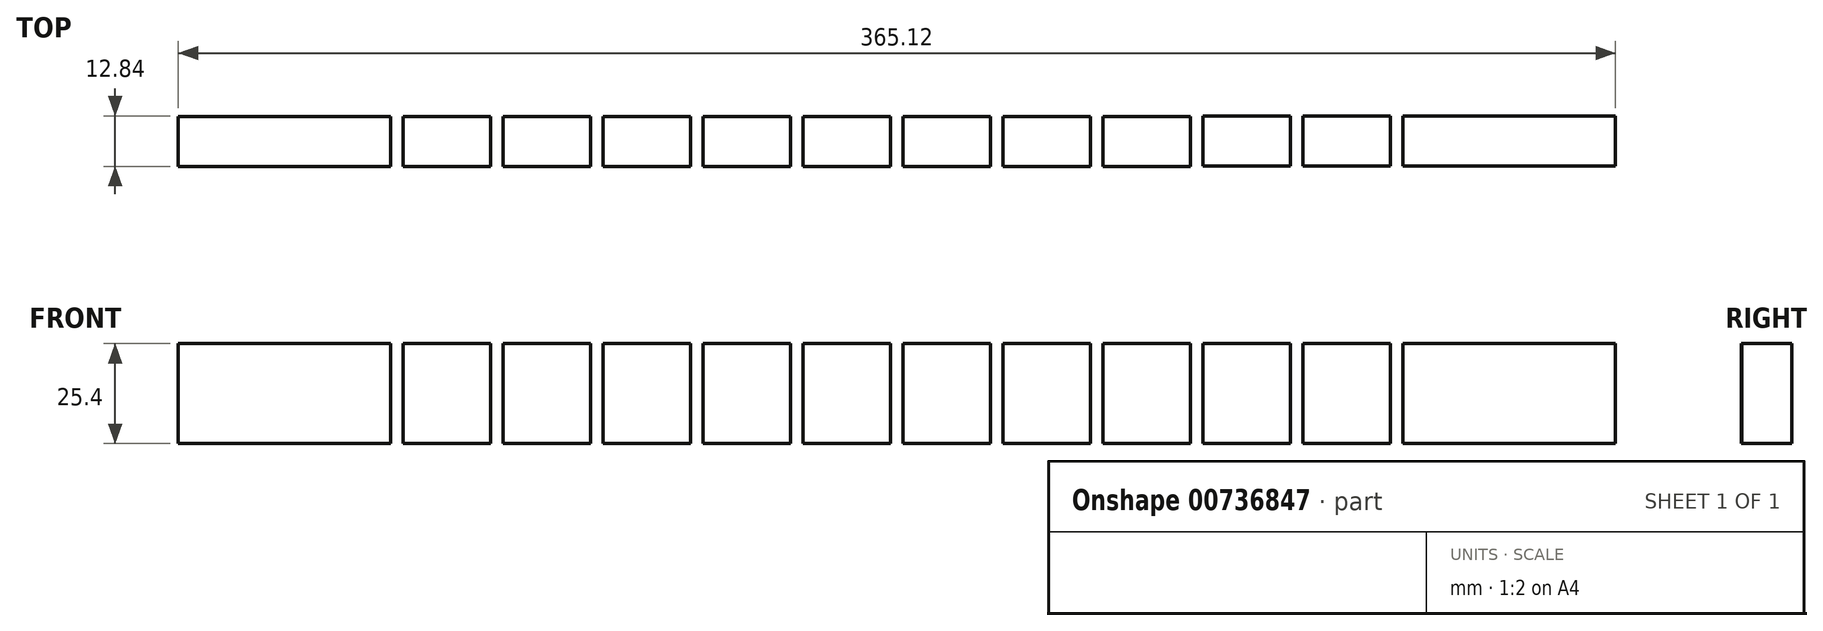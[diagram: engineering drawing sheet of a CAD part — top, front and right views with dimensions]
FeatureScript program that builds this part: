
annotation { "Feature Type Name" : "Feature", "Feature Type Description" : "" }
export const myFeature = defineFeature(function(context is Context, id is Id, definition is map)
    precondition{}
    {
        {
            var Q0;
            Q0=qCreatedBy(makeId("Top.planeOp"),FACE);
            var sketch = newSketch(context, id + "F0", { "sketchPlane" : qUnion([Q0])});
            skLineSegment(sketch, "E0.bottom", {"start": v(-126.46, 34.03) * mm, "end": v(-72.48, 34.03) * mm});
            skLineSegment(sketch, "E0.top", {"start": v(-126.46, 21.33) * mm, "end": v(-72.48, 21.33) * mm});
            skLineSegment(sketch, "E0.left", {"start": v(-126.46, 34.03) * mm, "end": v(-126.46, 21.33) * mm});
            skLineSegment(sketch, "E0.right", {"start": v(-72.48, 34.03) * mm, "end": v(-72.48, 21.33) * mm});
            skLineSegment(sketch, "E1.bottom", {"start": v(-69.3, 34.03) * mm, "end": v(-47.08, 34.03) * mm});
            skLineSegment(sketch, "E1.top", {"start": v(-69.3, 21.33) * mm, "end": v(-47.08, 21.33) * mm});
            skLineSegment(sketch, "E1.left", {"start": v(-69.3, 34.03) * mm, "end": v(-69.3, 21.33) * mm});
            skLineSegment(sketch, "E1.right", {"start": v(-47.08, 34.03) * mm, "end": v(-47.08, 21.33) * mm});
            skLineSegment(sketch, "E2.bottom", {"start": v(-43.9, 34.03) * mm, "end": v(-21.68, 34.03) * mm});
            skLineSegment(sketch, "E2.top", {"start": v(-43.9, 21.33) * mm, "end": v(-21.68, 21.33) * mm});
            skLineSegment(sketch, "E2.left", {"start": v(-43.9, 34.03) * mm, "end": v(-43.9, 21.33) * mm});
            skLineSegment(sketch, "E2.right", {"start": v(-21.68, 34.03) * mm, "end": v(-21.68, 21.33) * mm});
            skLineSegment(sketch, "E3.bottom", {"start": v(-18.5, 34.03) * mm, "end": v(3.72, 34.03) * mm});
            skLineSegment(sketch, "E3.top", {"start": v(-18.5, 21.33) * mm, "end": v(3.72, 21.33) * mm});
            skLineSegment(sketch, "E3.left", {"start": v(-18.5, 34.03) * mm, "end": v(-18.5, 21.33) * mm});
            skLineSegment(sketch, "E3.right", {"start": v(3.72, 34.03) * mm, "end": v(3.72, 21.33) * mm});
            skLineSegment(sketch, "E4.bottom", {"start": v(6.9, 34.03) * mm, "end": v(29.12, 34.03) * mm});
            skLineSegment(sketch, "E4.top", {"start": v(6.9, 21.33) * mm, "end": v(29.12, 21.33) * mm});
            skLineSegment(sketch, "E4.left", {"start": v(6.9, 34.03) * mm, "end": v(6.9, 21.33) * mm});
            skLineSegment(sketch, "E4.right", {"start": v(29.12, 34.03) * mm, "end": v(29.12, 21.33) * mm});
            skLineSegment(sketch, "E5.bottom", {"start": v(32.3, 34.03) * mm, "end": v(54.52, 34.03) * mm});
            skLineSegment(sketch, "E5.top", {"start": v(32.3, 21.33) * mm, "end": v(54.52, 21.33) * mm});
            skLineSegment(sketch, "E5.left", {"start": v(32.3, 34.03) * mm, "end": v(32.3, 21.33) * mm});
            skLineSegment(sketch, "E5.right", {"start": v(54.52, 34.03) * mm, "end": v(54.52, 21.33) * mm});
            skLineSegment(sketch, "E6.bottom", {"start": v(57.7, 34.03) * mm, "end": v(79.92, 34.03) * mm});
            skLineSegment(sketch, "E6.top", {"start": v(57.7, 21.33) * mm, "end": v(79.92, 21.33) * mm});
            skLineSegment(sketch, "E6.left", {"start": v(57.7, 34.03) * mm, "end": v(57.7, 21.33) * mm});
            skLineSegment(sketch, "E6.right", {"start": v(79.92, 34.03) * mm, "end": v(79.92, 21.33) * mm});
            skLineSegment(sketch, "E7.bottom", {"start": v(83.1, 34.03) * mm, "end": v(105.32, 34.03) * mm});
            skLineSegment(sketch, "E7.top", {"start": v(83.1, 21.33) * mm, "end": v(105.32, 21.33) * mm});
            skLineSegment(sketch, "E7.left", {"start": v(83.1, 34.03) * mm, "end": v(83.1, 21.33) * mm});
            skLineSegment(sketch, "E7.right", {"start": v(105.32, 34.03) * mm, "end": v(105.32, 21.33) * mm});
            skLineSegment(sketch, "E8.bottom", {"start": v(108.5, 34.03) * mm, "end": v(130.72, 34.03) * mm});
            skLineSegment(sketch, "E8.top", {"start": v(108.5, 21.33) * mm, "end": v(130.72, 21.33) * mm});
            skLineSegment(sketch, "E8.left", {"start": v(108.5, 34.03) * mm, "end": v(108.5, 21.33) * mm});
            skLineSegment(sketch, "E8.right", {"start": v(130.72, 34.03) * mm, "end": v(130.72, 21.33) * mm});
            skLineSegment(sketch, "E9.bottom", {"start": v(133.89, 34.17) * mm, "end": v(156.11, 34.17) * mm});
            skLineSegment(sketch, "E9.top", {"start": v(133.89, 21.47) * mm, "end": v(156.11, 21.47) * mm});
            skLineSegment(sketch, "E9.left", {"start": v(133.89, 34.17) * mm, "end": v(133.89, 21.47) * mm});
            skLineSegment(sketch, "E9.right", {"start": v(156.11, 34.17) * mm, "end": v(156.11, 21.47) * mm});
            skLineSegment(sketch, "E10.bottom", {"start": v(159.29, 34.17) * mm, "end": v(181.51, 34.17) * mm});
            skLineSegment(sketch, "E10.top", {"start": v(159.29, 21.47) * mm, "end": v(181.51, 21.47) * mm});
            skLineSegment(sketch, "E10.left", {"start": v(159.29, 34.17) * mm, "end": v(159.29, 21.47) * mm});
            skLineSegment(sketch, "E10.right", {"start": v(181.51, 34.17) * mm, "end": v(181.51, 21.47) * mm});
            skLineSegment(sketch, "E11.bottom", {"start": v(184.69, 34.17) * mm, "end": v(238.66, 34.17) * mm});
            skLineSegment(sketch, "E11.top", {"start": v(184.69, 21.47) * mm, "end": v(238.66, 21.47) * mm});
            skLineSegment(sketch, "E11.left", {"start": v(184.69, 34.17) * mm, "end": v(184.69, 21.47) * mm});
            skLineSegment(sketch, "E11.right", {"start": v(238.66, 34.17) * mm, "end": v(238.66, 21.47) * mm});
            skSolve(sketch);
        }
        {
            var Q0;
            Q0=makeQuery(id+"F0.imprint","IMPRINT",FACE,{"disambiguationData":[TD([[makeQuery(id+"F0.imprint","IMPRINT",EDGE,{"derivedFrom":sQuery(id+"F0.wireOp",EDGE,"E0.bottom")}),-1.0]])]});
            var Q1;
            Q1=makeQuery(id+"F0.imprint","IMPRINT",FACE,{"disambiguationData":[TD([[makeQuery(id+"F0.imprint","IMPRINT",EDGE,{"derivedFrom":sQuery(id+"F0.wireOp",EDGE,"E1.bottom")}),-1.0]])]});
            var Q2;
            Q2=makeQuery(id+"F0.imprint","IMPRINT",FACE,{"disambiguationData":[TD([[makeQuery(id+"F0.imprint","IMPRINT",EDGE,{"derivedFrom":sQuery(id+"F0.wireOp",EDGE,"E2.bottom")}),-1.0]])]});
            var Q3;
            Q3=makeQuery(id+"F0.imprint","IMPRINT",FACE,{"disambiguationData":[TD([[makeQuery(id+"F0.imprint","IMPRINT",EDGE,{"derivedFrom":sQuery(id+"F0.wireOp",EDGE,"E3.bottom")}),-1.0]])]});
            var Q4;
            Q4=makeQuery(id+"F0.imprint","IMPRINT",FACE,{"disambiguationData":[TD([[makeQuery(id+"F0.imprint","IMPRINT",EDGE,{"derivedFrom":sQuery(id+"F0.wireOp",EDGE,"E4.bottom")}),-1.0]])]});
            var Q5;
            Q5=makeQuery(id+"F0.imprint","IMPRINT",FACE,{"disambiguationData":[TD([[makeQuery(id+"F0.imprint","IMPRINT",EDGE,{"derivedFrom":sQuery(id+"F0.wireOp",EDGE,"E5.bottom")}),-1.0]])]});
            var Q6;
            Q6=makeQuery(id+"F0.imprint","IMPRINT",FACE,{"disambiguationData":[TD([[makeQuery(id+"F0.imprint","IMPRINT",EDGE,{"derivedFrom":sQuery(id+"F0.wireOp",EDGE,"E6.bottom")}),-1.0]])]});
            var Q7;
            Q7=makeQuery(id+"F0.imprint","IMPRINT",FACE,{"disambiguationData":[TD([[makeQuery(id+"F0.imprint","IMPRINT",EDGE,{"derivedFrom":sQuery(id+"F0.wireOp",EDGE,"E7.bottom")}),-1.0]])]});
            var Q8;
            Q8=makeQuery(id+"F0.imprint","IMPRINT",FACE,{"disambiguationData":[TD([[makeQuery(id+"F0.imprint","IMPRINT",EDGE,{"derivedFrom":sQuery(id+"F0.wireOp",EDGE,"E8.bottom")}),-1.0]])]});
            var Q9;
            Q9=makeQuery(id+"F0.imprint","IMPRINT",FACE,{"disambiguationData":[TD([[makeQuery(id+"F0.imprint","IMPRINT",EDGE,{"derivedFrom":sQuery(id+"F0.wireOp",EDGE,"E9.bottom")}),-1.0]])]});
            var Q10;
            Q10=makeQuery(id+"F0.imprint","IMPRINT",FACE,{"disambiguationData":[TD([[makeQuery(id+"F0.imprint","IMPRINT",EDGE,{"derivedFrom":sQuery(id+"F0.wireOp",EDGE,"E11.bottom")}),-1.0]])]});
            var Q11;
            Q11=makeQuery(id+"F0.imprint","IMPRINT",FACE,{"disambiguationData":[TD([[makeQuery(id+"F0.imprint","IMPRINT",EDGE,{"derivedFrom":sQuery(id+"F0.wireOp",EDGE,"E10.bottom")}),-1.0]])]});
            extrude(context, id + "F1", {"entities" : qUnion([Q0, Q1, Q2, Q3, Q4, Q5, Q6, Q7, Q8, Q9, Q10, Q11]), "depth" : 25.4 * mm, "offsetDistance" : 25.4 * mm});
        }
    });
